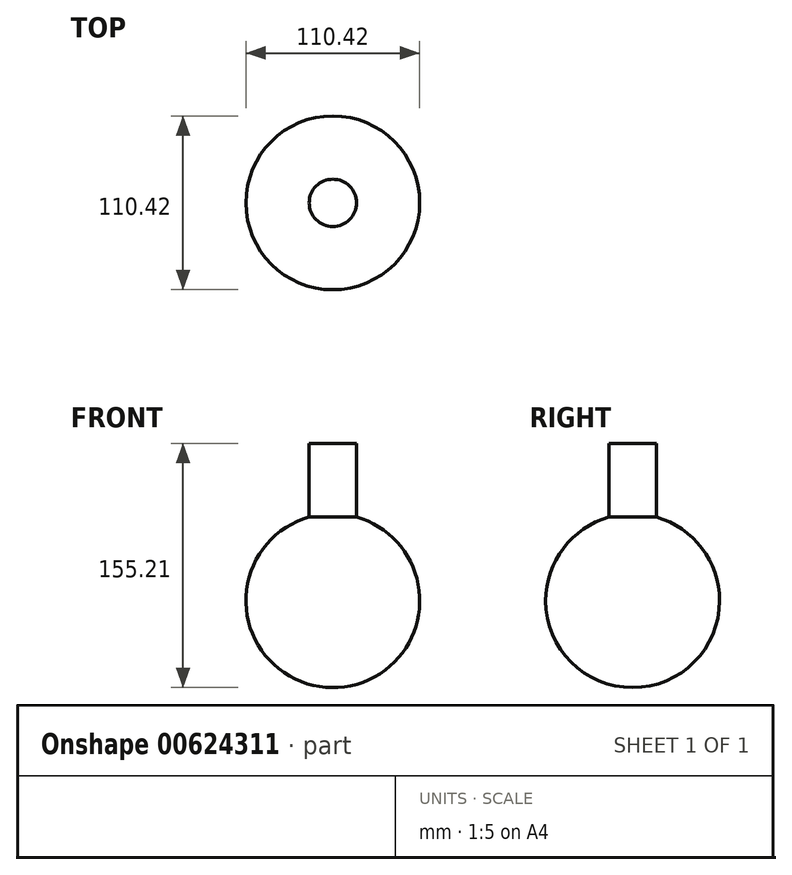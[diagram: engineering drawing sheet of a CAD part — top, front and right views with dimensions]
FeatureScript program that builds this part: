
annotation { "Feature Type Name" : "Feature", "Feature Type Description" : "" }
export const myFeature = defineFeature(function(context is Context, id is Id, definition is map)
    precondition{}
    {
        {
            var Q0;
            Q0=qCreatedBy(makeId("Top.planeOp"),FACE);
            var sketch = newSketch(context, id + "F0", { "sketchPlane" : qUnion([Q0])});
            skArc(sketch, "E0", {"start": v(0, -55.2) * mm, "mid": v(55.2, 0) * mm, "end": v(0, 55.2) * mm});
            skLineSegment(sketch, "E1", {"start": v(0, 0) * mm, "end": v(0, -102.84) * mm});
            skLineSegment(sketch, "E2", {"start": v(0, -102.84) * mm, "end": v(0, 73.63) * mm});
            skSolve(sketch);
        }
        {
            var Q0;
            {var subQ0=sQuery(id+"F0.wireOp",EDGE,"E0");Q0=makeQuery(id+"F0.imprint","IMPRINT",FACE,{"disambiguationData":[TD([[makeQuery(id+"F0.imprint","IMPRINT",EDGE,{"derivedFrom":subQ0}),1.0]])]});}
            var Q1;
            Q1=sQuery(id+"F0.wireOp",EDGE,"E2");
            revolve(context, id + "F1", {"entities" : qUnion([Q0]), "axis" : qUnion([Q1]), "revolveType" : RevolveType.FULL});
        }
        {
            var Q0;
            Q0=qCreatedBy(makeId("Top.planeOp"),FACE);
            var sketch = newSketch(context, id + "F2", { "sketchPlane" : qUnion([Q0])});
            skCircle(sketch, "E3", {"center": v(0, 0) * mm, "radius": 15 * mm});
            skSolve(sketch);
        }
        {
            var Q0;
            Q0 = qSketchRegion(id + "F2", true);
            extrude(context, id + "F3", {"entities" : qUnion([Q0]), "operationType" : NewBodyOperationType.ADD, "depth" : 100 * mm, "offsetDistance" : 25 * mm});
        }
    });
